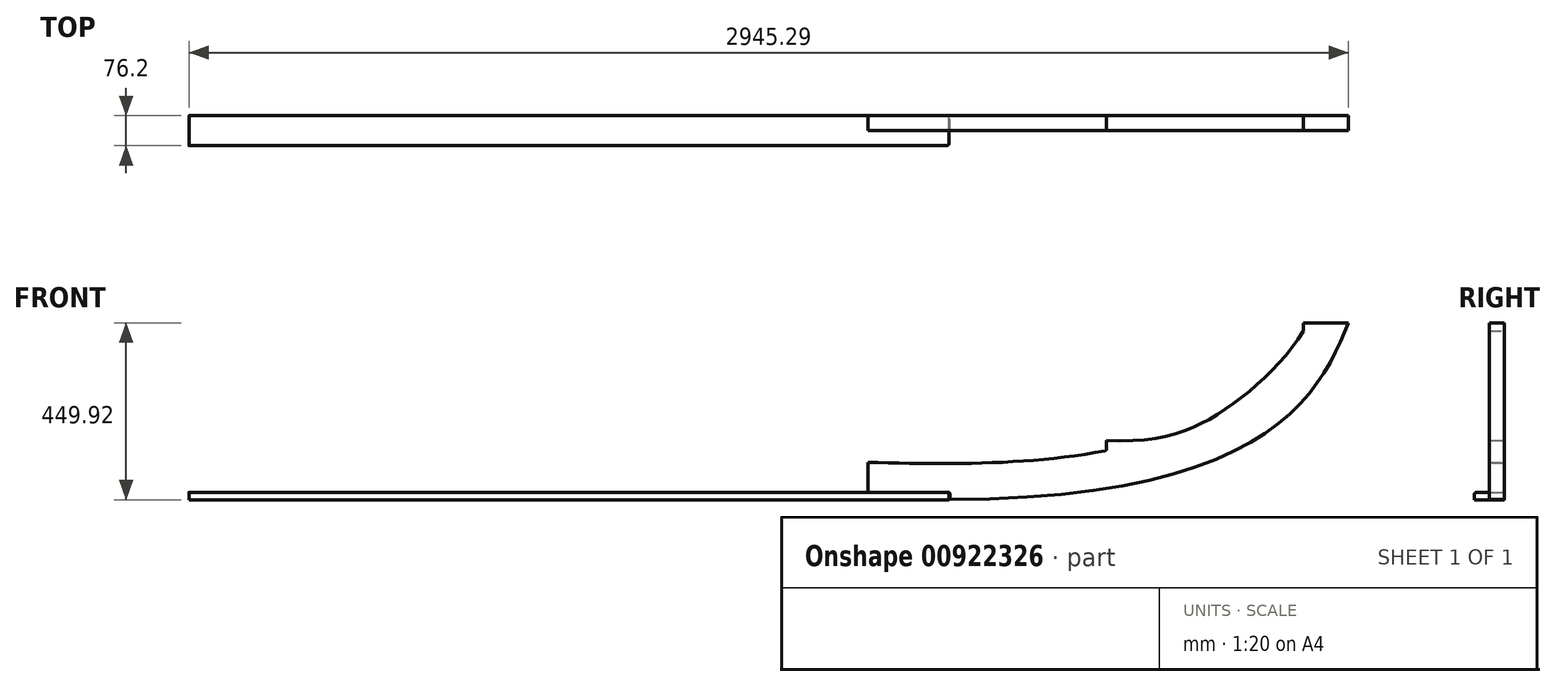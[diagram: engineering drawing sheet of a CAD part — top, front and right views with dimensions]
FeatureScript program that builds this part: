
annotation { "Feature Type Name" : "Feature", "Feature Type Description" : "" }
export const myFeature = defineFeature(function(context is Context, id is Id, definition is map)
    precondition{}
    {
        {
            var Q0;
            Q0=qCreatedBy(makeId("Front.planeOp"),FACE);
            var sketch = newSketch(context, id + "F0", { "sketchPlane" : qUnion([Q0])});
            skLineSegment(sketch, "E0", {"start": v(614.32, 411.44) * mm, "end": v(499.6, 411.44) * mm});
            skLineSegment(sketch, "E1", {"start": v(499.6, 411.44) * mm, "end": v(499.6, 390.5) * mm});
            skFitSpline(sketch, "E2", {"points": [v(-0.08, 112.57) * mm, v(294.36, 187.11) * mm, v(499.6, 390.5) * mm], "startDerivative": vector(824.1, -45.49) * mm, "endDerivative": vector(295.2, 488.42) * mm});
            skLineSegment(sketch, "E3", {"start": v(-606.63, -19.09) * mm, "end": v(-402.98, -19.09) * mm});
            skLineSegment(sketch, "E4", {"start": v(-397.9, -24.17) * mm, "end": v(-397.9, -37.29) * mm});
            skFitSpline(sketch, "E5", {"points": [v(-397.9, -37.29) * mm, v(614.32, 411.44) * mm], "startDerivative": vector(2426.16, 0.36) * mm, "endDerivative": vector(216.06, 545.12) * mm});
            skLineSegment(sketch, "E6", {"start": v(-606.63, -19.09) * mm, "end": v(-606.63, 57.11) * mm});
            skLineSegment(sketch, "E7", {"start": v(-0.08, 112.57) * mm, "end": v(-0.08, 91.36) * mm});
            skFitSpline(sketch, "E8", {"points": [v(-606.63, 57.11) * mm, v(-0.08, 87.17) * mm], "startDerivative": vector(610.22, -17.06) * mm, "endDerivative": vector(592.52, 115.34) * mm});
            skPoint(sketch, "E9.visualSharp", {"position": v(-397.9, -19.09) * mm});
            skArc(sketch, "E9.filletArc", {"start": v(-397.9, -24.17) * mm, "mid": v(-399.4, -20.58) * mm, "end": v(-402.98, -19.09) * mm});
            skArc(sketch, "E10.filletArc", {"start": v(-4.2, 86.37) * mm, "mid": v(-1.25, 88.12) * mm, "end": v(-0.08, 91.36) * mm});
            skSolve(sketch);
        }
        {
            var Q0;
            Q0=makeQuery(id+"F0.imprint","IMPRINT",FACE,{"disambiguationData":[TD([[makeQuery(id+"F0.imprint","IMPRINT",EDGE,{"derivedFrom":sQuery(id+"F0.wireOp",EDGE,"E0")}),1.0]])]});
            extrude(context, id + "F1", {"entities" : qUnion([Q0]), "depth" : 38.1 * mm, "offsetDistance" : 25.4 * mm});
        }
        {
            var Q0;
            Q0=qCreatedBy(makeId("Front.planeOp"),FACE);
            var sketch = newSketch(context, id + "F2", { "sketchPlane" : qUnion([Q0])});
            skLineSegment(sketch, "E11", {"start": v(-400.57, -38.48) * mm, "end": v(-400.57, -19.5) * mm});
            skLineSegment(sketch, "E12", {"start": v(-400.57, -19.5) * mm, "end": v(-2330.97, -19.5) * mm});
            skLineSegment(sketch, "E13", {"start": v(-2330.97, -19.5) * mm, "end": v(-2330.97, -38.36) * mm});
            skLineSegment(sketch, "E14", {"start": v(-2330.97, -38.36) * mm, "end": v(-400.57, -38.48) * mm});
            skSolve(sketch);
        }
        {
            var Q0;
            Q0=makeQuery(id+"F2.imprint","IMPRINT",FACE,{"disambiguationData":[TD([[makeQuery(id+"F2.imprint","IMPRINT",EDGE,{"derivedFrom":sQuery(id+"F2.wireOp",EDGE,"E11")}),1.0]])]});
            var Q1;
            Q1 = qSketchRegion(id + "F2", true);
            extrude(context, id + "F3", {"entities" : qUnion([Q0, Q1]), "depth" : 76.2 * mm, "offsetDistance" : 25.4 * mm});
        }
        {
            var Q0;
            Q0=makeQuery(id+"F3.opExtrude","SWEPT_EDGE",EDGE,{"disambiguationData":[OSD([sQuery(id+"F2.wireOp",EDGE,"E11"),sQuery(id+"F2.wireOp",EDGE,"E12")])]});
            fillet(context, id + "F4", {"entities" : qUnion([Q0]), "radius" : 5.08 * mm, "tangentPropagation" : true, "allowEdgeOverflow" : false});
        }
        {
            var Q0;
            Q0=makeQuery(id+"F3.opExtrude","CAP_EDGE",EDGE,{"disambiguationData":[OSD([sQuery(id+"F2.wireOp",EDGE,"E12")])],"isStart":false});
            fillet(context, id + "F5", {"entities" : qUnion([Q0]), "radius" : 5.08 * mm, "tangentPropagation" : true, "allowEdgeOverflow" : false});
        }
        {
            var Q0;
            Q0=makeQuery(id+"F3.opExtrude","CAP_EDGE",EDGE,{"disambiguationData":[OSD([sQuery(id+"F2.wireOp",EDGE,"E12")])],"isStart":true});
            fillet(context, id + "F6", {"entities" : qUnion([Q0]), "radius" : 5.08 * mm, "tangentPropagation" : true, "allowEdgeOverflow" : false});
        }
    });
